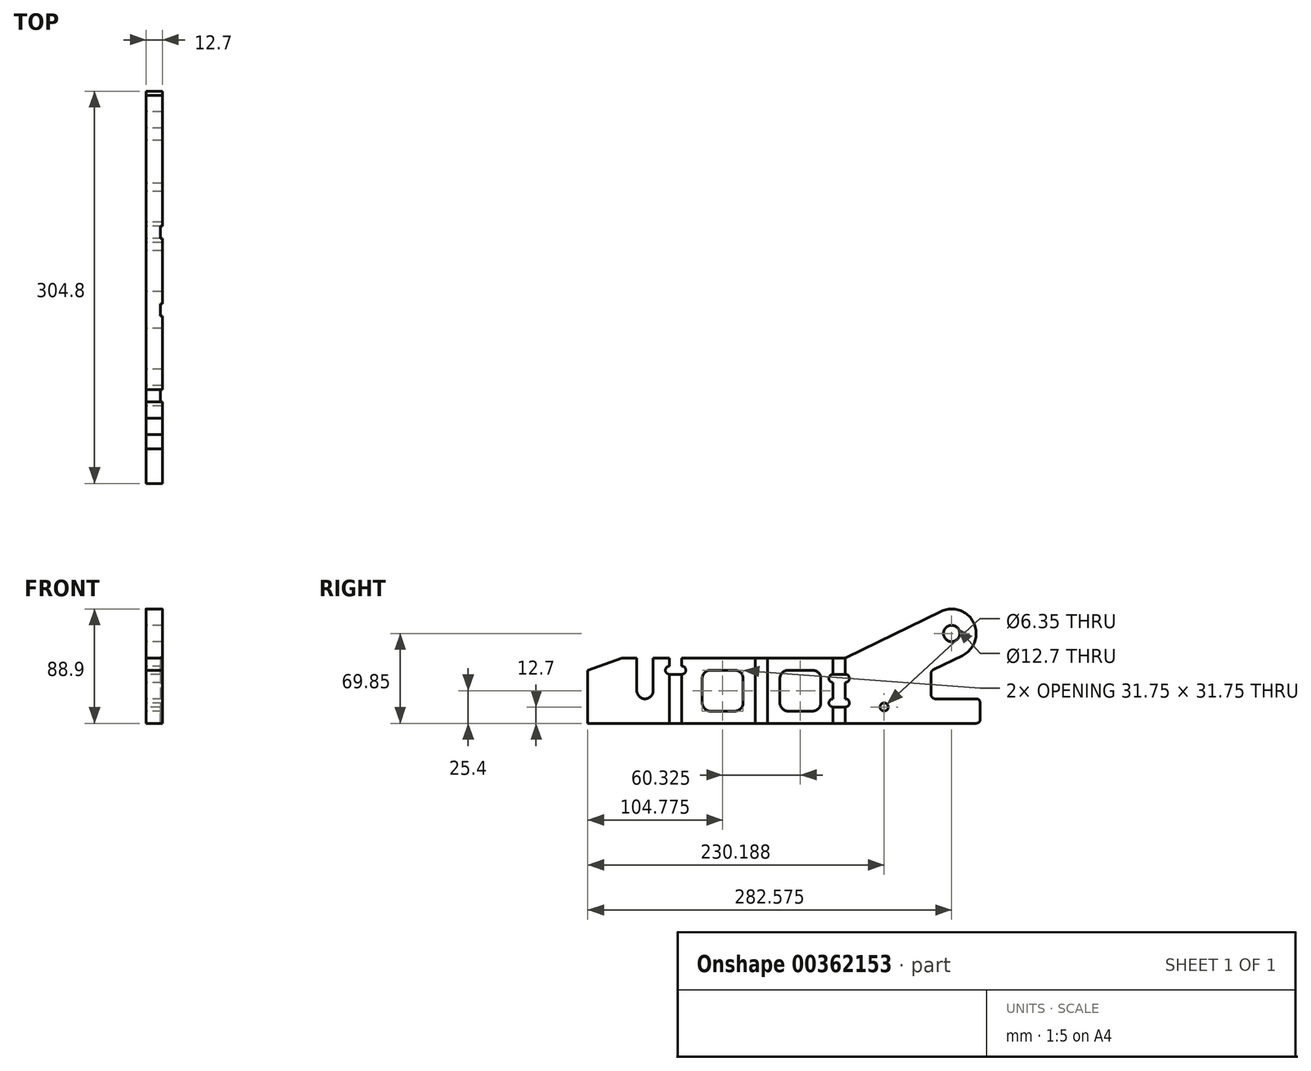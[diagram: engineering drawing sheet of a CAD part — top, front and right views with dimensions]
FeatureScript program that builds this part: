
annotation { "Feature Type Name" : "Feature", "Feature Type Description" : "" }
export const myFeature = defineFeature(function(context is Context, id is Id, definition is map)
    precondition{}
    {
        {
            var Q0;
            Q0=qCreatedBy(makeId("Right.planeOp"),FACE);
            var sketch = newSketch(context, id + "F0", { "sketchPlane" : qUnion([Q0])});
            skLineSegment(sketch, "E0", {"start": v(0, 0) * mm, "end": v(0, 41.28) * mm});
            skLineSegment(sketch, "E1", {"start": v(0, 41.28) * mm, "end": v(26.72, 50.8) * mm});
            skLineSegment(sketch, "E2", {"start": v(26.72, 50.8) * mm, "end": v(200.03, 50.8) * mm});
            skLineSegment(sketch, "E3", {"start": v(200.03, 50.8) * mm, "end": v(274.23, 86.97) * mm});
            skArc(sketch, "E4", {"start": v(290.92, 52.73) * mm, "mid": v(299.7, 78.2) * mm, "end": v(274.23, 86.97) * mm});
            skLineSegment(sketch, "E5", {"start": v(0, 0) * mm, "end": v(304.8, 0) * mm});
            skLineSegment(sketch, "E6", {"start": v(304.8, 0) * mm, "end": v(304.8, 19.05) * mm});
            skLineSegment(sketch, "E7", {"start": v(304.8, 19.05) * mm, "end": v(266.7, 19.05) * mm});
            skLineSegment(sketch, "E8", {"start": v(266.7, 19.05) * mm, "end": v(266.7, 40.92) * mm});
            skLineSegment(sketch, "E9", {"start": v(266.7, 40.92) * mm, "end": v(290.92, 52.73) * mm});
            skPoint(sketch, "E10", {"position": v(44.45, 25.4) * mm});
            skLineSegment(sketch, "E11", {"start": v(44.45, 25.4) * mm, "end": v(44.45, 50.8) * mm, "construction": true});
            skLineSegment(sketch, "E12", {"start": v(44.45, 25.4) * mm, "end": v(44.45, 0) * mm, "construction": true});
            skCircle(sketch, "E13", {"center": v(44.45, 25.4) * mm, "radius": 38.1 * mm, "construction": true});
            skLineSegment(sketch, "E14", {"start": v(38.1, 50.8) * mm, "end": v(38.1, 25.4) * mm});
            skArc(sketch, "E15", {"start": v(38.1, 25.4) * mm, "mid": v(44.45, 19.05) * mm, "end": v(50.8, 25.4) * mm});
            skLineSegment(sketch, "E16", {"start": v(50.8, 25.4) * mm, "end": v(50.8, 50.8) * mm});
            skLineSegment(sketch, "E17", {"start": v(44.45, 38.1) * mm, "end": v(63.5, 38.1) * mm, "construction": true});
            skLineSegment(sketch, "E18", {"start": v(63.5, 38.1) * mm, "end": v(73.02, 38.1) * mm});
            skLineSegment(sketch, "E19", {"start": v(73.02, 50.8) * mm, "end": v(73.02, 44.45) * mm});
            skLineSegment(sketch, "E20", {"start": v(63.5, 50.8) * mm, "end": v(63.5, 44.45) * mm});
            skArc(sketch, "E21", {"start": v(63.5, 44.45) * mm, "mid": v(60.32, 41.27) * mm, "end": v(63.5, 38.1) * mm});
            skArc(sketch, "E22", {"start": v(73.02, 38.1) * mm, "mid": v(76.2, 41.27) * mm, "end": v(73.02, 44.45) * mm});
            skLineSegment(sketch, "E23", {"start": v(130.17, 50.8) * mm, "end": v(130.17, 0) * mm});
            skLineSegment(sketch, "E24", {"start": v(44.45, -12.7) * mm, "end": v(304.8, -12.7) * mm, "construction": true});
            skLineSegment(sketch, "E25", {"start": v(139.7, 50.8) * mm, "end": v(139.7, 0) * mm});
            skCircle(sketch, "E26", {"center": v(230.19, 12.7) * mm, "radius": 25.4 * mm, "construction": true});
            skCircle(sketch, "E27", {"center": v(230.19, 12.7) * mm, "radius": 3.18 * mm});
            skLineSegment(sketch, "E28", {"start": v(260.35, 0) * mm, "end": v(260.35, -3.2) * mm, "construction": true});
            skLineSegment(sketch, "E29", {"start": v(260.35, 0) * mm, "end": v(266.7, 0) * mm, "construction": true});
            skLineSegment(sketch, "E30", {"start": v(266.7, 0) * mm, "end": v(266.7, 75.3) * mm, "construction": true});
            skLineSegment(sketch, "E31", {"start": v(298.45, 19.05) * mm, "end": v(298.45, 9.52) * mm, "construction": true});
            skLineSegment(sketch, "E32", {"start": v(298.45, 9.52) * mm, "end": v(298.45, 0) * mm, "construction": true});
            skLineSegment(sketch, "E33", {"start": v(285.75, 9.52) * mm, "end": v(298.45, 9.52) * mm, "construction": true});
            skCircle(sketch, "E34", {"center": v(282.58, 69.85) * mm, "radius": 6.35 * mm});
            skLineSegment(sketch, "E35", {"start": v(200.03, 38.1) * mm, "end": v(190.5, 38.1) * mm});
            skLineSegment(sketch, "E36", {"start": v(190.5, 12.7) * mm, "end": v(200.03, 12.7) * mm});
            skLineSegment(sketch, "E37", {"start": v(190.5, 38.1) * mm, "end": v(190.5, 50.8) * mm, "construction": true});
            skLineSegment(sketch, "E38", {"start": v(190.5, 50.8) * mm, "end": v(189.86, 50.7) * mm, "construction": true});
            skLineSegment(sketch, "E39", {"start": v(190.5, 12.7) * mm, "end": v(190.5, 0) * mm, "construction": true});
            skArc(sketch, "E40", {"start": v(190.5, 19.05) * mm, "mid": v(187.32, 15.88) * mm, "end": v(190.5, 12.7) * mm});
            skArc(sketch, "E41", {"start": v(190.5, 38.1) * mm, "mid": v(187.32, 34.93) * mm, "end": v(190.5, 31.75) * mm});
            skLineSegment(sketch, "E42", {"start": v(190.5, 31.75) * mm, "end": v(190.5, 19.05) * mm});
            skArc(sketch, "E43", {"start": v(200.03, 12.7) * mm, "mid": v(203.2, 15.88) * mm, "end": v(200.03, 19.05) * mm});
            skArc(sketch, "E44", {"start": v(200.03, 31.75) * mm, "mid": v(203.2, 34.92) * mm, "end": v(200.03, 38.1) * mm});
            skLineSegment(sketch, "E45", {"start": v(200.03, 19.05) * mm, "end": v(200.03, 31.75) * mm});
            skLineSegment(sketch, "E46", {"start": v(200.03, 38.1) * mm, "end": v(200.03, 50.8) * mm, "construction": true});
            skLineSegment(sketch, "E47", {"start": v(130.17, 25.4) * mm, "end": v(139.7, 25.4) * mm, "construction": true});
            skLineSegment(sketch, "E48", {"start": v(134.94, 25.4) * mm, "end": v(134.94, 50.8) * mm, "construction": true});
            skLineSegment(sketch, "E49", {"start": v(134.94, 50.8) * mm, "end": v(134.94, 25.4) * mm, "construction": true});
            skLineSegment(sketch, "E50", {"start": v(134.94, 25.4) * mm, "end": v(134.94, 0) * mm, "construction": true});
            skPoint(sketch, "E51", {"position": v(134.94, 12.7) * mm});
            skPoint(sketch, "E52", {"position": v(134.94, 25.4) * mm});
            skPoint(sketch, "E53", {"position": v(134.94, 38.1) * mm});
            skCircle(sketch, "E54", {"center": v(282.58, 69.85) * mm, "radius": 76.2 * mm, "construction": true});
            skLineSegment(sketch, "E55", {"start": v(256.99, 141.62) * mm, "end": v(31.66, 61.29) * mm, "construction": true});
            skLineSegment(sketch, "E56", {"start": v(31.66, 61.29) * mm, "end": v(0, 50) * mm, "construction": true});
            skLineSegment(sketch, "E57", {"start": v(282.58, 69.85) * mm, "end": v(279.8, 75.56) * mm, "construction": true});
            skLineSegment(sketch, "E58", {"start": v(282.58, 69.85) * mm, "end": v(285.36, 64.14) * mm, "construction": true});
            skPoint(sketch, "E59", {"position": v(288.14, 58.43) * mm});
            skLineSegment(sketch, "E60", {"start": v(285.36, 64.14) * mm, "end": v(288.14, 58.43) * mm, "construction": true});
            skLineSegment(sketch, "E61", {"start": v(282.58, 69.85) * mm, "end": v(276.87, 67.07) * mm, "construction": true});
            skLineSegment(sketch, "E62", {"start": v(276.87, 67.07) * mm, "end": v(271.16, 64.28) * mm, "construction": true});
            skLineSegment(sketch, "E63", {"start": v(282.58, 69.85) * mm, "end": v(288.28, 72.63) * mm, "construction": true});
            skLineSegment(sketch, "E64", {"start": v(288.28, 72.63) * mm, "end": v(294, 75.42) * mm, "construction": true});
            skPoint(sketch, "E65", {"position": v(271.16, 64.28) * mm});
            skPoint(sketch, "E66", {"position": v(294, 75.42) * mm});
            skLineSegment(sketch, "E67", {"start": v(200.03, 12.7) * mm, "end": v(200.03, 0) * mm, "construction": true});
            skLineSegment(sketch, "E68", {"start": v(230.19, 12.7) * mm, "end": v(260.35, 12.7) * mm, "construction": true});
            skLineSegment(sketch, "E69", {"start": v(230.19, 12.7) * mm, "end": v(200.03, 12.7) * mm, "construction": true});
            skPoint(sketch, "E70", {"position": v(285.75, 9.52) * mm});
            skPoint(sketch, "E71", {"position": v(298.45, 9.52) * mm});
            skLineSegment(sketch, "E72", {"start": v(263.53, 20.64) * mm, "end": v(263.53, 41.28) * mm, "construction": true});
            skLineSegment(sketch, "E73", {"start": v(263.53, 20.64) * mm, "end": v(263.53, 0) * mm, "construction": true});
            skPoint(sketch, "E74", {"position": v(263.53, 30.96) * mm});
            skPoint(sketch, "E75", {"position": v(263.53, 20.64) * mm});
            skPoint(sketch, "E76", {"position": v(263.53, 10.32) * mm});
            skLineSegment(sketch, "E77", {"start": v(260.35, 20.64) * mm, "end": v(266.7, 20.64) * mm, "construction": true});
            skLineSegment(sketch, "E78", {"start": v(266.7, 41.28) * mm, "end": v(260.35, 41.28) * mm, "construction": true});
            skLineSegment(sketch, "E79.bottom", {"start": v(120.65, 41.27) * mm, "end": v(88.9, 41.27) * mm});
            skLineSegment(sketch, "E79.top", {"start": v(120.65, 9.52) * mm, "end": v(88.9, 9.52) * mm});
            skLineSegment(sketch, "E79.left", {"start": v(120.65, 41.27) * mm, "end": v(120.65, 9.52) * mm});
            skLineSegment(sketch, "E79.right", {"start": v(88.9, 41.27) * mm, "end": v(88.9, 9.53) * mm});
            skLineSegment(sketch, "E80.bottom", {"start": v(149.22, 41.28) * mm, "end": v(180.97, 41.28) * mm});
            skLineSegment(sketch, "E80.top", {"start": v(149.22, 9.53) * mm, "end": v(180.97, 9.53) * mm});
            skLineSegment(sketch, "E80.left", {"start": v(149.22, 41.28) * mm, "end": v(149.22, 9.52) * mm});
            skLineSegment(sketch, "E80.right", {"start": v(180.97, 41.27) * mm, "end": v(180.97, 9.53) * mm});
            skLineSegment(sketch, "E81", {"start": v(120.65, 41.27) * mm, "end": v(120.65, 50.8) * mm, "construction": true});
            skLineSegment(sketch, "E82", {"start": v(120.65, 41.28) * mm, "end": v(130.17, 41.28) * mm, "construction": true});
            skLineSegment(sketch, "E83", {"start": v(149.22, 41.28) * mm, "end": v(139.7, 41.28) * mm, "construction": true});
            skLineSegment(sketch, "E84", {"start": v(149.22, 41.28) * mm, "end": v(149.22, 50.8) * mm, "construction": true});
            skLineSegment(sketch, "E85", {"start": v(120.65, 9.52) * mm, "end": v(120.65, 0) * mm, "construction": true});
            skSolve(sketch);
        }
        {
            var Q0;
            Q0=makeQuery(id+"F0.imprint","IMPRINT",FACE,{"disambiguationData":[TD([[makeQuery(id+"F0.imprint","IMPRINT",EDGE,{"derivedFrom":sQuery(id+"F0.wireOp",EDGE,"E0")}),-1.0]])]});
            var Q1;
            {var subQ0=sQuery(id+"F0.wireOp",EDGE,"E23");Q1=makeQuery(id+"F0.imprint","IMPRINT",FACE,{"disambiguationData":[TD([[makeQuery(id+"F0.imprint","IMPRINT",EDGE,{"derivedFrom":subQ0}),1.0]])]});}
            var Q2;
            {var subQ2=sQuery(id+"F0.wireOp",EDGE,"E3");Q2=makeQuery(id+"F0.imprint","IMPRINT",FACE,{"disambiguationData":[TD([[makeQuery(id+"F0.imprint","IMPRINT",EDGE,{"derivedFrom":subQ2}),-1.0]])]});}
            extrude(context, id + "F1", {"entities" : qUnion([Q0, Q1, Q2]), "depth" : 12.7 * mm});
        }
        {
            var Q0;
            Q0=makeQuery(id+"F1.opExtrude","SWEPT_EDGE",EDGE,{"disambiguationData":[OSD([sQuery(id+"F0.wireOp",EDGE,"E2"),sQuery(id+"F0.wireOp",EDGE,"E3")])]});
            var Q1;
            Q1=makeQuery(id+"F1.opExtrude","SWEPT_EDGE",EDGE,{"disambiguationData":[OSD([sQuery(id+"F0.wireOp",EDGE,"E8"),sQuery(id+"F0.wireOp",EDGE,"E9")])]});
            var Q2;
            Q2=makeQuery(id+"F1.opExtrude","SWEPT_EDGE",EDGE,{"disambiguationData":[OSD([sQuery(id+"F0.wireOp",EDGE,"E7"),sQuery(id+"F0.wireOp",EDGE,"E8")])]});
            var Q3;
            Q3=makeQuery(id+"F1.opExtrude","SWEPT_EDGE",EDGE,{"disambiguationData":[OSD([sQuery(id+"F0.wireOp",EDGE,"E6"),sQuery(id+"F0.wireOp",EDGE,"E7")])]});
            var Q4;
            Q4=makeQuery(id+"F1.opExtrude","SWEPT_EDGE",EDGE,{"disambiguationData":[OSD([sQuery(id+"F0.wireOp",EDGE,"E5"),sQuery(id+"F0.wireOp",EDGE,"E6")])]});
            fillet(context, id + "F2", {"entities" : qUnion([Q0, Q1, Q2, Q3, Q4]), "radius" : 3.17 * mm, "tangentPropagation" : true, "allowEdgeOverflow" : false});
        }
        {
            var Q0;
            Q0=makeQuery(id+"F1.opExtrude","CAP_FACE",FACE,{"disambiguationData":[OSD([sQuery(id+"F0.wireOp",EDGE,"E0"),sQuery(id+"F0.wireOp",EDGE,"E1"),sQuery(id+"F0.wireOp",EDGE,"E2"),sQuery(id+"F0.wireOp",EDGE,"E3"),sQuery(id+"F0.wireOp",EDGE,"E4"),sQuery(id+"F0.wireOp",EDGE,"E5"),sQuery(id+"F0.wireOp",EDGE,"E6"),sQuery(id+"F0.wireOp",EDGE,"E7"),sQuery(id+"F0.wireOp",EDGE,"E8"),sQuery(id+"F0.wireOp",EDGE,"E9"),sQuery(id+"F0.wireOp",EDGE,"E14"),sQuery(id+"F0.wireOp",EDGE,"E15"),sQuery(id+"F0.wireOp",EDGE,"E16"),sQuery(id+"F0.wireOp",EDGE,"E18"),sQuery(id+"F0.wireOp",EDGE,"E19"),sQuery(id+"F0.wireOp",EDGE,"E20"),sQuery(id+"F0.wireOp",EDGE,"E21"),sQuery(id+"F0.wireOp",EDGE,"E22"),sQuery(id+"F0.wireOp",EDGE,"E27"),sQuery(id+"F0.wireOp",EDGE,"1B4OWH7D-hY2x-AemJ-kr1P-dbijIKMEHeJH"),sQuery(id+"F0.wireOp",EDGE,"vXDJeEpz-HHiL-fvMT-sxGg-cfHU6cQA9n6z"),sQuery(id+"F0.wireOp",EDGE,"E34"),sQuery(id+"F0.wireOp",EDGE,"E35"),sQuery(id+"F0.wireOp",EDGE,"E36"),sQuery(id+"F0.wireOp",EDGE,"E40"),sQuery(id+"F0.wireOp",EDGE,"E41"),sQuery(id+"F0.wireOp",EDGE,"E42"),sQuery(id+"F0.wireOp",EDGE,"E43"),sQuery(id+"F0.wireOp",EDGE,"E44"),sQuery(id+"F0.wireOp",EDGE,"E45")])],"isStart":false});
            var sketch = newSketch(context, id + "F3", { "sketchPlane" : qUnion([Q0])});
            skLineSegment(sketch, "E86.bottom", {"start": v(63.5, 38.1) * mm, "end": v(73.02, 38.1) * mm});
            skLineSegment(sketch, "E86.top", {"start": v(63.5, 0) * mm, "end": v(73.02, 0) * mm});
            skLineSegment(sketch, "E86.left", {"start": v(63.5, 38.1) * mm, "end": v(63.5, 0) * mm});
            skLineSegment(sketch, "E86.right", {"start": v(73.02, 38.1) * mm, "end": v(73.02, 0) * mm});
            skSolve(sketch);
        }
        {
            var Q0;
            Q0=makeQuery(id+"F3.imprint","IMPRINT",FACE,{"disambiguationData":[TD([[makeQuery(id+"F3.imprint","IMPRINT",EDGE,{"derivedFrom":sQuery(id+"F3.wireOp",EDGE,"E86.bottom")}),-1.0]])]});
            extrude(context, id + "F4", {"entities" : qUnion([Q0]), "operationType" : NewBodyOperationType.REMOVE, "oppositeDirection" : true, "depth" : 1.59 * mm});
        }
        {
            var Q0;
            {var subQ0=sQuery(id+"F0.wireOp",EDGE,"E40");var subQ1=sQuery(id+"F0.wireOp",EDGE,"E36");var subQ2=sQuery(id+"F0.wireOp",EDGE,"E35");var subQ3=sQuery(id+"F0.wireOp",EDGE,"E34");var subQ4=sQuery(id+"F0.wireOp",EDGE,"vXDJeEpz-HHiL-fvMT-sxGg-cfHU6cQA9n6z");var subQ5=sQuery(id+"F0.wireOp",EDGE,"1B4OWH7D-hY2x-AemJ-kr1P-dbijIKMEHeJH");var subQ6=sQuery(id+"F0.wireOp",EDGE,"E27");var subQ7=sQuery(id+"F0.wireOp",EDGE,"E44");var subQ8=sQuery(id+"F0.wireOp",EDGE,"E5");var subQ9=sQuery(id+"F0.wireOp",EDGE,"E43");var subQ10=sQuery(id+"F0.wireOp",EDGE,"E4");var subQ11=sQuery(id+"F0.wireOp",EDGE,"E42");var subQ12=sQuery(id+"F0.wireOp",EDGE,"E3");var subQ13=sQuery(id+"F0.wireOp",EDGE,"E19");var subQ14=sQuery(id+"F0.wireOp",EDGE,"E41");var subQ15=sQuery(id+"F0.wireOp",EDGE,"E2");var subQ16=sQuery(id+"F0.wireOp",EDGE,"E45");var subQ17=sQuery(id+"F0.wireOp",EDGE,"E6");var subQ18=sQuery(id+"F0.wireOp",EDGE,"E22");var subQ19=sQuery(id+"F0.wireOp",EDGE,"E7");var subQ20=sQuery(id+"F0.wireOp",EDGE,"E8");var subQ21=sQuery(id+"F0.wireOp",EDGE,"E9");Q0=makeQuery(id+"F4.boolean.opBoolean","SPLIT",FACE,{"disambiguationData":[TD([makeQuery(id+"F1.opExtrude","SWEPT_FACE",FACE,{"disambiguationData":[OSD([subQ12])]})])],"derivedFrom":makeQuery(id+"F1.opExtrude","CAP_FACE",FACE,{"disambiguationData":[OSD([sQuery(id+"F0.wireOp",EDGE,"E0"),sQuery(id+"F0.wireOp",EDGE,"E1"),subQ15,subQ12,subQ10,subQ8,subQ17,subQ19,subQ20,subQ21,sQuery(id+"F0.wireOp",EDGE,"E14"),sQuery(id+"F0.wireOp",EDGE,"E15"),sQuery(id+"F0.wireOp",EDGE,"E16"),sQuery(id+"F0.wireOp",EDGE,"E18"),subQ13,sQuery(id+"F0.wireOp",EDGE,"E20"),sQuery(id+"F0.wireOp",EDGE,"E21"),subQ18,subQ6,subQ5,subQ4,subQ3,subQ2,subQ1,subQ0,subQ14,subQ11,subQ9,subQ7,subQ16])],"isStart":false})});}
            var sketch = newSketch(context, id + "F5", { "sketchPlane" : qUnion([Q0])});
            skLineSegment(sketch, "E87.bottom", {"start": v(200.03, 0) * mm, "end": v(190.5, 0) * mm});
            skLineSegment(sketch, "E87.top", {"start": v(200.03, 52.1) * mm, "end": v(190.5, 52.1) * mm});
            skLineSegment(sketch, "E87.left", {"start": v(200.03, 0) * mm, "end": v(200.03, 52.1) * mm});
            skLineSegment(sketch, "E87.right", {"start": v(190.5, 0) * mm, "end": v(190.5, 52.1) * mm});
            skSolve(sketch);
        }
        {
            var Q0;
            {var subQ0=sQuery(id+"F5.wireOp",EDGE,"E87.bottom");Q0=makeQuery(id+"F5.imprint","IMPRINT",FACE,{"disambiguationData":[TD([[makeQuery(id+"F5.imprint","IMPRINT",EDGE,{"derivedFrom":subQ0}),1.0]])]});}
            var Q1;
            {var subQ0=sQuery(id+"F5.wireOp",EDGE,"E87.top");Q1=makeQuery(id+"F5.imprint","IMPRINT",FACE,{"disambiguationData":[TD([[makeQuery(id+"F5.imprint","IMPRINT",EDGE,{"derivedFrom":subQ0}),-1.0]])]});}
            var Q2;
            {var subQ0=sQuery(id+"F0.wireOp",EDGE,"E35");var subQ1=makeQuery(id+"F1.opExtrude","CAP_EDGE",EDGE,{"disambiguationData":[OSD([subQ0])],"isStart":false});Q2=makeQuery(id+"F5.imprint","IMPRINT",FACE,{"disambiguationData":[TD([[makeQuery(id+"F5.imprint","IMPRINT",EDGE,{"derivedFrom":subQ1}),-1.0]])]});}
            extrude(context, id + "F6", {"entities" : qUnion([Q0, Q1, Q2]), "operationType" : NewBodyOperationType.REMOVE, "oppositeDirection" : true, "depth" : 1.59 * mm});
        }
        {
            var Q0;
            {var subQ0=sQuery(id+"F0.wireOp",EDGE,"E19");var subQ1=makeQuery(id+"F1.opExtrude","SWEPT_FACE",FACE,{"disambiguationData":[OSD([subQ0])]});var subQ2=sQuery(id+"F0.wireOp",EDGE,"E41");var subQ4=sQuery(id+"F0.wireOp",EDGE,"E5");var subQ6=sQuery(id+"F0.wireOp",EDGE,"E22");var subQ8=sQuery(id+"F0.wireOp",EDGE,"E3");var subQ9=sQuery(id+"F0.wireOp",EDGE,"E2");var subQ16=sQuery(id+"F0.wireOp",EDGE,"E40");var subQ19=sQuery(id+"F0.wireOp",EDGE,"E42");var subQ22=sQuery(id+"F0.wireOp",EDGE,"E36");var subQ23=sQuery(id+"F0.wireOp",EDGE,"E45");var subQ24=sQuery(id+"F0.wireOp",EDGE,"E44");var subQ25=sQuery(id+"F0.wireOp",EDGE,"E43");var subQ26=sQuery(id+"F0.wireOp",EDGE,"E35");var subQ27=sQuery(id+"F0.wireOp",EDGE,"E34");var subQ28=sQuery(id+"F0.wireOp",EDGE,"vXDJeEpz-HHiL-fvMT-sxGg-cfHU6cQA9n6z");var subQ29=sQuery(id+"F0.wireOp",EDGE,"1B4OWH7D-hY2x-AemJ-kr1P-dbijIKMEHeJH");var subQ30=sQuery(id+"F0.wireOp",EDGE,"E27");var subQ31=sQuery(id+"F0.wireOp",EDGE,"E9");var subQ32=sQuery(id+"F0.wireOp",EDGE,"E8");var subQ33=sQuery(id+"F0.wireOp",EDGE,"E7");var subQ34=sQuery(id+"F0.wireOp",EDGE,"E6");var subQ35=sQuery(id+"F0.wireOp",EDGE,"E4");var subQ36=makeQuery(id+"F1.opExtrude","CAP_FACE",FACE,{"disambiguationData":[OSD([sQuery(id+"F0.wireOp",EDGE,"E0"),sQuery(id+"F0.wireOp",EDGE,"E1"),subQ9,subQ8,subQ35,subQ4,subQ34,subQ33,subQ32,subQ31,sQuery(id+"F0.wireOp",EDGE,"E14"),sQuery(id+"F0.wireOp",EDGE,"E15"),sQuery(id+"F0.wireOp",EDGE,"E16"),sQuery(id+"F0.wireOp",EDGE,"E18"),subQ0,sQuery(id+"F0.wireOp",EDGE,"E20"),sQuery(id+"F0.wireOp",EDGE,"E21"),subQ6,subQ30,subQ29,subQ28,subQ27,subQ26,subQ22,subQ16,subQ2,subQ19,subQ25,subQ24,subQ23])],"isStart":false});Q0=makeQuery(id+"F6.boolean.opBoolean","SPLIT",FACE,{"disambiguationData":[TD([subQ1])],"derivedFrom":makeQuery(id+"F4.boolean.opBoolean","SPLIT",FACE,{"disambiguationData":[TD([makeQuery(id+"F1.opExtrude","SWEPT_FACE",FACE,{"disambiguationData":[OSD([subQ8])]})])],"derivedFrom":subQ36})});}
            var sketch = newSketch(context, id + "F7", { "sketchPlane" : qUnion([Q0])});
            skLineSegment(sketch, "E88.bottom", {"start": v(130.17, 50.8) * mm, "end": v(139.7, 50.8) * mm});
            skLineSegment(sketch, "E88.top", {"start": v(130.17, 0) * mm, "end": v(139.7, 0) * mm});
            skLineSegment(sketch, "E88.left", {"start": v(130.17, 50.8) * mm, "end": v(130.17, 0) * mm});
            skLineSegment(sketch, "E88.right", {"start": v(139.7, 50.8) * mm, "end": v(139.7, 0) * mm});
            skLineSegment(sketch, "E89", {"start": v(134.94, 50.8) * mm, "end": v(134.94, 25.4) * mm, "construction": true});
            skLineSegment(sketch, "E90", {"start": v(134.94, 25.4) * mm, "end": v(134.94, 0) * mm, "construction": true});
            skPoint(sketch, "E91", {"position": v(134.94, 38.1) * mm});
            skPoint(sketch, "E92", {"position": v(134.94, 25.4) * mm});
            skPoint(sketch, "E93", {"position": v(134.94, 12.7) * mm});
            skSolve(sketch);
        }
        {
            var Q0;
            Q0=makeQuery(id+"F7.imprint","IMPRINT",FACE,{"disambiguationData":[TD([[makeQuery(id+"F7.imprint","IMPRINT",EDGE,{"derivedFrom":sQuery(id+"F7.wireOp",EDGE,"E88.bottom")}),-1.0]])]});
            extrude(context, id + "F8", {"entities" : qUnion([Q0]), "operationType" : NewBodyOperationType.REMOVE, "oppositeDirection" : true, "depth" : 1.59 * mm});
        }
        {
            var Q0;
            Q0=makeQuery(id+"F1.opExtrude","SWEPT_EDGE",EDGE,{"disambiguationData":[OSD([sQuery(id+"F0.wireOp",EDGE,"E79.bottom"),sQuery(id+"F0.wireOp",EDGE,"E79.right")])]});
            var Q1;
            Q1=makeQuery(id+"F1.opExtrude","SWEPT_EDGE",EDGE,{"disambiguationData":[OSD([sQuery(id+"F0.wireOp",EDGE,"E79.bottom"),sQuery(id+"F0.wireOp",EDGE,"E79.left")])]});
            var Q2;
            Q2=makeQuery(id+"F1.opExtrude","SWEPT_EDGE",EDGE,{"disambiguationData":[OSD([sQuery(id+"F0.wireOp",EDGE,"E80.bottom"),sQuery(id+"F0.wireOp",EDGE,"E80.right")])]});
            var Q3;
            Q3=makeQuery(id+"F1.opExtrude","SWEPT_EDGE",EDGE,{"disambiguationData":[OSD([sQuery(id+"F0.wireOp",EDGE,"E80.bottom"),sQuery(id+"F0.wireOp",EDGE,"E80.left")])]});
            var Q4;
            Q4=makeQuery(id+"F1.opExtrude","SWEPT_EDGE",EDGE,{"disambiguationData":[OSD([sQuery(id+"F0.wireOp",EDGE,"E80.top"),sQuery(id+"F0.wireOp",EDGE,"E80.left")])]});
            var Q5;
            Q5=makeQuery(id+"F1.opExtrude","SWEPT_EDGE",EDGE,{"disambiguationData":[OSD([sQuery(id+"F0.wireOp",EDGE,"E79.top"),sQuery(id+"F0.wireOp",EDGE,"E79.right")])]});
            var Q6;
            Q6=makeQuery(id+"F1.opExtrude","SWEPT_EDGE",EDGE,{"disambiguationData":[OSD([sQuery(id+"F0.wireOp",EDGE,"E80.top"),sQuery(id+"F0.wireOp",EDGE,"E80.right")])]});
            var Q7;
            Q7=makeQuery(id+"F1.opExtrude","SWEPT_EDGE",EDGE,{"disambiguationData":[OSD([sQuery(id+"F0.wireOp",EDGE,"E79.top"),sQuery(id+"F0.wireOp",EDGE,"E79.left")])]});
            fillet(context, id + "F9", {"entities" : qUnion([Q0, Q1, Q2, Q3, Q4, Q5, Q6, Q7]), "radius" : 6.35 * mm, "tangentPropagation" : true, "allowEdgeOverflow" : false});
        }
    });
